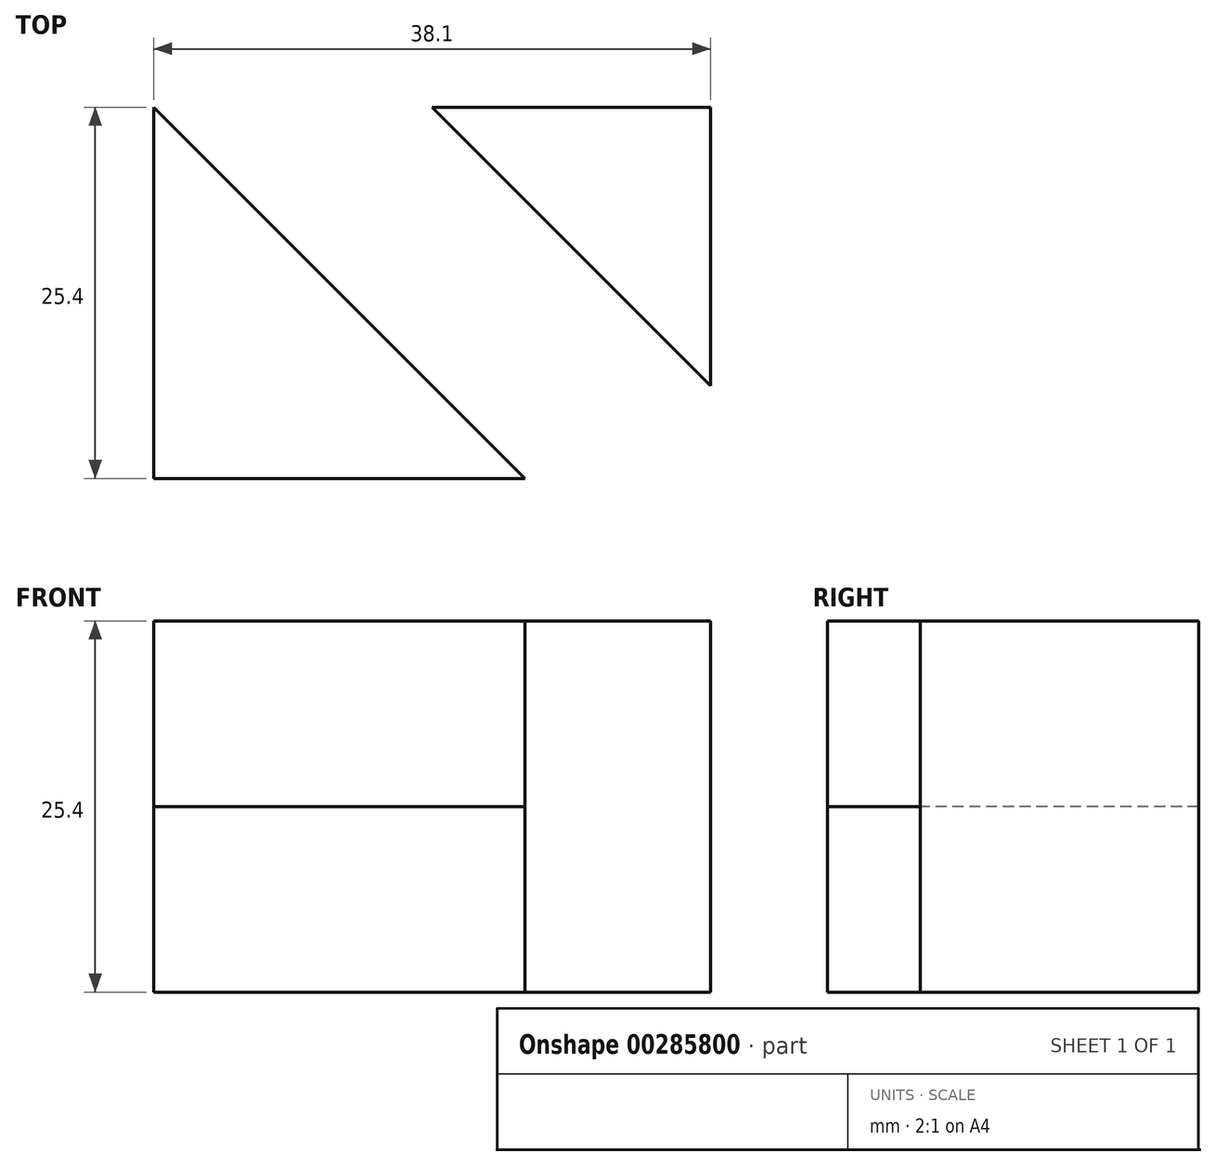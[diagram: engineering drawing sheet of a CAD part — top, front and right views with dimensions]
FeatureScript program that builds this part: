
annotation { "Feature Type Name" : "Feature", "Feature Type Description" : "" }
export const myFeature = defineFeature(function(context is Context, id is Id, definition is map)
    precondition{}
    {
        {
            var Q0;
            Q0=qCreatedBy(makeId("Top.planeOp"),FACE);
            var sketch = newSketch(context, id + "F0", { "sketchPlane" : qUnion([Q0])});
            skLineSegment(sketch, "E0.bottom", {"start": v(-19.05, 25.4) * mm, "end": v(19.05, 25.4) * mm});
            skLineSegment(sketch, "E0.top", {"start": v(-19.05, 0) * mm, "end": v(19.05, 0) * mm});
            skLineSegment(sketch, "E0.left", {"start": v(-19.05, 25.4) * mm, "end": v(-19.05, 0) * mm});
            skLineSegment(sketch, "E0.right", {"start": v(19.05, 25.4) * mm, "end": v(19.05, 0) * mm});
            skLineSegment(sketch, "E1", {"start": v(-19.05, 25.4) * mm, "end": v(6.35, 0) * mm});
            skLineSegment(sketch, "E2", {"start": v(6.35, 0) * mm, "end": v(-19.05, 0) * mm});
            skLineSegment(sketch, "E3", {"start": v(-19.05, 25.4) * mm, "end": v(0, 25.4) * mm});
            skLineSegment(sketch, "E4", {"start": v(0, 25.4) * mm, "end": v(19.05, 6.35) * mm});
            skLineSegment(sketch, "E5", {"start": v(19.05, 6.35) * mm, "end": v(19.05, 0) * mm});
            skSolve(sketch);
        }
        {
            var Q0;
            Q0=makeQuery(id+"F0.imprint","IMPRINT",FACE,{"disambiguationData":[TD([[makeQuery(id+"F0.imprint","IMPRINT",EDGE,{"derivedFrom":sQuery(id+"F0.wireOp",EDGE,"E0.left")}),1.0]])]});
            var Q1;
            Q1=makeQuery(id+"F0.imprint","IMPRINT",FACE,{"disambiguationData":[TD([[makeQuery(id+"F0.imprint","IMPRINT",EDGE,{"derivedFrom":sQuery(id+"F0.wireOp",EDGE,"E0.bottom")}),-1.0]])]});
            extrude(context, id + "F1", {"entities" : qUnion([Q0, Q1]), "depth" : 25.4 * mm});
        }
        {
            var Q0;
            Q0=makeQuery(id+"F0.imprint","IMPRINT",FACE,{"disambiguationData":[TD([[makeQuery(id+"F0.imprint","IMPRINT",EDGE,{"derivedFrom":sQuery(id+"F0.wireOp",EDGE,"E0.top")}),1.0]])]});
            extrude(context, id + "F2", {"entities" : qUnion([Q0]), "depth" : 12.7 * mm});
        }
    });
